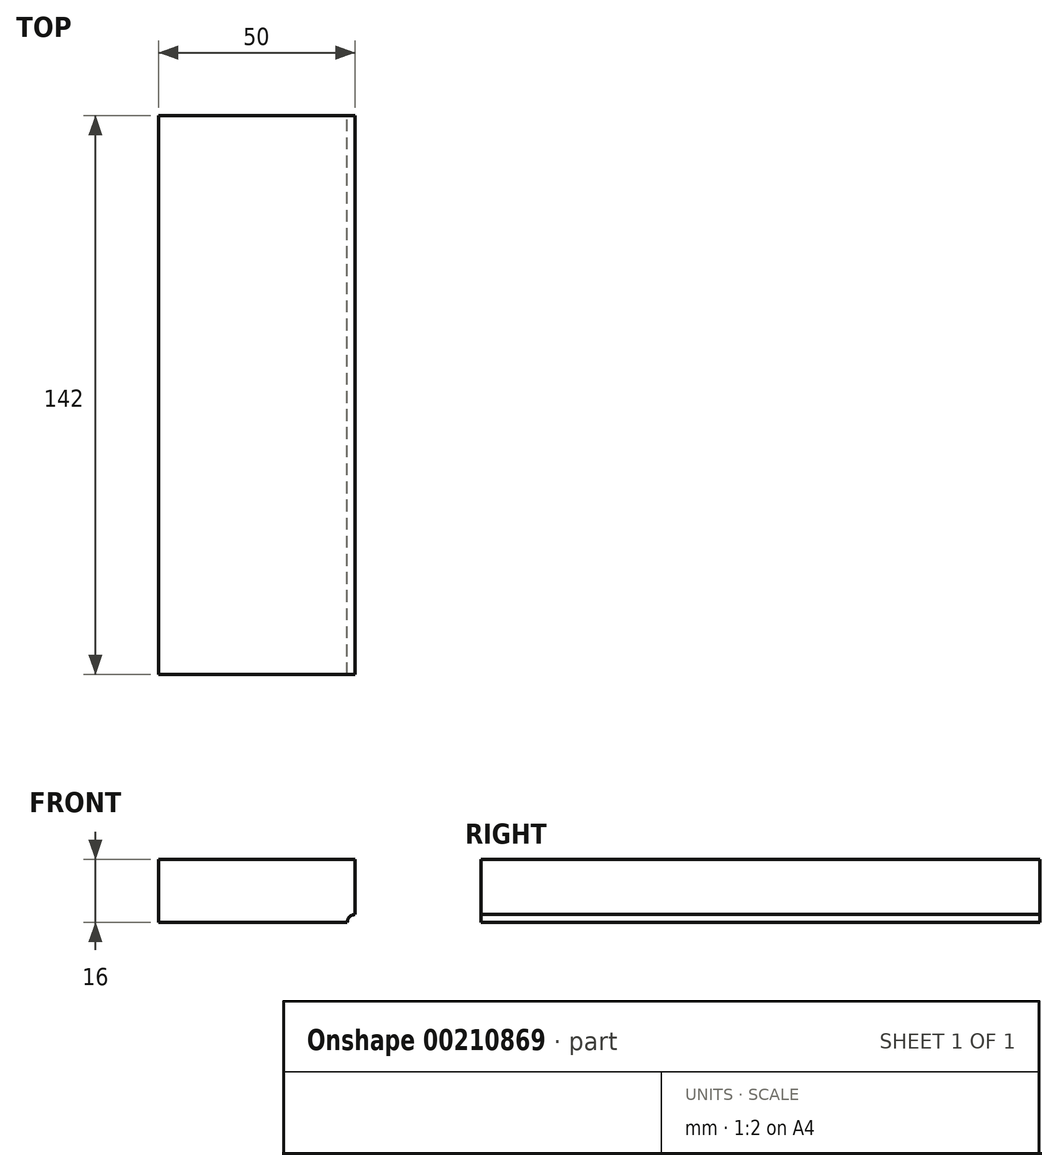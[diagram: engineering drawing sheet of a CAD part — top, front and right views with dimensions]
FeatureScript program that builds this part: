
annotation { "Feature Type Name" : "Feature", "Feature Type Description" : "" }
export const myFeature = defineFeature(function(context is Context, id is Id, definition is map)
    precondition{}
    {
        {
            var Q0;
            Q0=qCreatedBy(makeId("Front.planeOp"),FACE);
            var sketch = newSketch(context, id + "F0", { "sketchPlane" : qUnion([Q0])});
            skLineSegment(sketch, "E0.bottom", {"start": v(25, 8) * mm, "end": v(-25, 8) * mm});
            skLineSegment(sketch, "E0.top", {"start": v(23, -8) * mm, "end": v(-25, -8) * mm});
            skLineSegment(sketch, "E0.left", {"start": v(25, 8) * mm, "end": v(25, -6) * mm});
            skLineSegment(sketch, "E0.right", {"start": v(-25, 8) * mm, "end": v(-25, -8) * mm});
            skPoint(sketch, "E0.middle", {"position": v(0, 0) * mm});
            skArc(sketch, "E1", {"start": v(25, -6) * mm, "mid": v(23.59, -6.59) * mm, "end": v(23, -8) * mm});
            skSolve(sketch);
        }
        {
            var Q0;
            Q0=makeQuery(id+"F0.imprint","IMPRINT",FACE,{"disambiguationData":[TD([[makeQuery(id+"F0.imprint","IMPRINT",EDGE,{"derivedFrom":sQuery(id+"F0.wireOp",EDGE,"E0.bottom")}),1.0]])]});
            extrude(context, id + "F1", {"entities" : qUnion([Q0]), "endBound" : BoundingType.SYMMETRIC, "depth" : 142 * mm});
        }
    });
